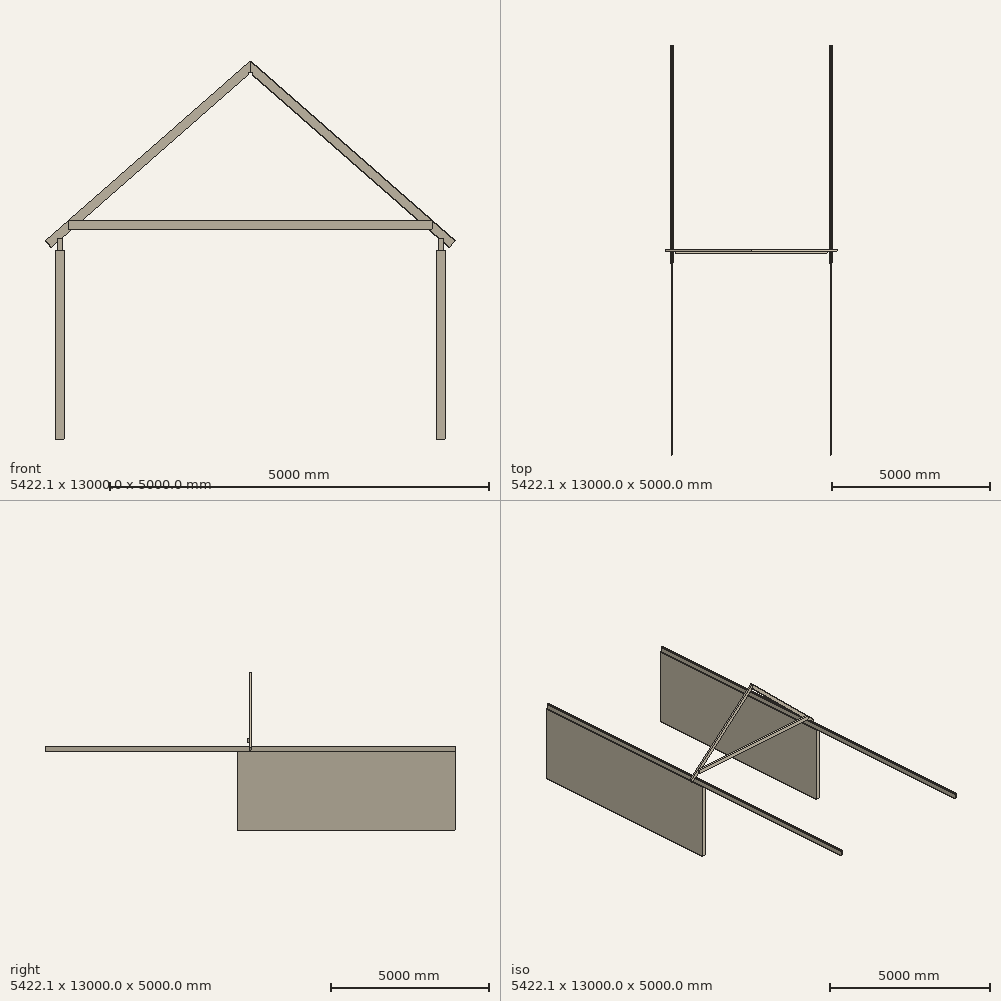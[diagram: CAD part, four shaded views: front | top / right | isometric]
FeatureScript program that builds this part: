
annotation { "Feature Type Name" : "Feature", "Feature Type Description" : "" }
export const myFeature = defineFeature(function(context is Context, id is Id, definition is map)
    precondition{}
    {
        {
            var Q0;
            Q0=qCreatedBy(makeId("Front.planeOp"),FACE);
            var sketch = newSketch(context, id + "F0", { "sketchPlane" : qUnion([Q0])});
            skLineSegment(sketch, "E0", {"start": v(0, 0) * mm, "end": v(0, 3904.1) * mm, "construction": true});
            skLineSegment(sketch, "E1", {"start": v(-3356.12, 0) * mm, "end": v(3820.43, 0) * mm, "construction": true});
            skLineSegment(sketch, "E2.bottom", {"start": v(-2550, 160) * mm, "end": v(-2490, 160) * mm});
            skLineSegment(sketch, "E2.top", {"start": v(-2550, 0) * mm, "end": v(-2490, 0) * mm});
            skLineSegment(sketch, "E2.left", {"start": v(-2550, 160) * mm, "end": v(-2550, 0) * mm});
            skLineSegment(sketch, "E2.right", {"start": v(-2490, 160) * mm, "end": v(-2490, 0) * mm});
            skLineSegment(sketch, "E3.bottom", {"start": v(2490, 160) * mm, "end": v(2550, 160) * mm});
            skLineSegment(sketch, "E3.top", {"start": v(2490, 0) * mm, "end": v(2550, 0) * mm});
            skLineSegment(sketch, "E3.left", {"start": v(2490, 160) * mm, "end": v(2490, 0) * mm});
            skLineSegment(sketch, "E3.right", {"start": v(2550, 160) * mm, "end": v(2550, 0) * mm});
            skLineSegment(sketch, "E4", {"start": v(-735.63, 2500) * mm, "end": v(730.19, 2500) * mm, "construction": true});
            skSolve(sketch);
        }
        {
            var Q0;
            Q0 = qSketchRegion(id + "F0", true);
            extrude(context, id + "F1", {"entities" : qUnion([Q0]), "endBound" : BoundingType.SYMMETRIC, "depth" : 13000 * mm, "offsetDistance" : 25 * mm});
        }
        {
            var Q0;
            Q0=makeQuery(id+"F1.opExtrude","CAP_FACE",FACE,{"disambiguationData":[OSD([sQuery(id+"F0.wireOp",EDGE,"E3.bottom"),sQuery(id+"F0.wireOp",EDGE,"E3.top"),sQuery(id+"F0.wireOp",EDGE,"E3.left"),sQuery(id+"F0.wireOp",EDGE,"E3.right")])],"isStart":true});
            var sketch = newSketch(context, id + "F2", { "sketchPlane" : qUnion([Q0])});
            skLineSegment(sketch, "E5.bottom", {"start": v(-2580, 0) * mm, "end": v(-2460, 0) * mm});
            skLineSegment(sketch, "E5.top", {"start": v(-2580, -2500) * mm, "end": v(-2460, -2500) * mm});
            skLineSegment(sketch, "E5.left", {"start": v(-2580, 0) * mm, "end": v(-2580, -2500) * mm});
            skLineSegment(sketch, "E5.right", {"start": v(-2460, 0) * mm, "end": v(-2460, -2500) * mm});
            skLineSegment(sketch, "E6.bottom", {"start": v(2460, 0) * mm, "end": v(2580, 0) * mm});
            skLineSegment(sketch, "E6.top", {"start": v(2460, -2500) * mm, "end": v(2580, -2500) * mm});
            skLineSegment(sketch, "E6.left", {"start": v(2460, 0) * mm, "end": v(2460, -2500) * mm});
            skLineSegment(sketch, "E6.right", {"start": v(2580, 0) * mm, "end": v(2580, -2500) * mm});
            skLineSegment(sketch, "E7", {"start": v(-2724.2, 0) * mm, "end": v(2884.68, 0) * mm, "construction": true});
            skPoint(sketch, "E7.startSnap0", {"position": v(-2520, 0) * mm});
            skSolve(sketch);
        }
        {
            var Q0;
            Q0 = qSketchRegion(id + "F2", true);
            extrude(context, id + "F3", {"entities" : qUnion([Q0]), "oppositeDirection" : true, "depth" : 6900 * mm, "offsetDistance" : 25 * mm});
        }
        {
            var Q0;
            Q0=qCreatedBy(makeId("Front.planeOp"),FACE);
            var sketch = newSketch(context, id + "F4", { "sketchPlane" : qUnion([Q0])});
            skLineSegment(sketch, "E8", {"start": v(-5, 2500) * mm, "end": v(-2711.05, 125.7) * mm});
            skLineSegment(sketch, "E9", {"start": v(-2711.05, 125.7) * mm, "end": v(-2631.9, 35.5) * mm});
            skLineSegment(sketch, "E10.bottom", {"start": v(-30, 2358.42) * mm, "end": v(30, 2358.42) * mm, "construction": true});
            skLineSegment(sketch, "E10.top", {"start": v(-30, 2198.42) * mm, "end": v(30, 2198.42) * mm, "construction": true});
            skLineSegment(sketch, "E10.left", {"start": v(-30, 2358.42) * mm, "end": v(-30, 2198.42) * mm, "construction": true});
            skLineSegment(sketch, "E10.right", {"start": v(30, 2358.42) * mm, "end": v(30, 2198.42) * mm, "construction": true});
            skLineSegment(sketch, "E11", {"start": v(-5, 2500) * mm, "end": v(-5, 2358.42) * mm});
            skLineSegment(sketch, "E12", {"start": v(-5, 2358.42) * mm, "end": v(-30, 2358.42) * mm});
            skLineSegment(sketch, "E13", {"start": v(-30, 2358.42) * mm, "end": v(-30, 2318.42) * mm});
            skLineSegment(sketch, "E14", {"start": v(-2550, 160) * mm, "end": v(-2550, 107.36) * mm});
            skLineSegment(sketch, "E15.trimOffspring", {"start": v(-2490, 160) * mm, "end": v(-30, 2318.42) * mm});
            skLineSegment(sketch, "E16", {"start": v(-2550, 160) * mm, "end": v(-2490, 160) * mm});
            skLineSegment(sketch, "E17", {"start": v(-2550, 107.36) * mm, "end": v(-2631.9, 35.5) * mm});
            skLineSegment(sketch, "E18.MirrorCS", {"start": v(2711.05, 125.7) * mm, "end": v(2631.9, 35.5) * mm});
            skLineSegment(sketch, "E19.MirrorCS", {"start": v(5, 2500) * mm, "end": v(2711.05, 125.7) * mm});
            skLineSegment(sketch, "E20.MirrorCS", {"start": v(2550, 107.36) * mm, "end": v(2631.9, 35.5) * mm});
            skLineSegment(sketch, "E21.MirrorCS", {"start": v(2550, 160) * mm, "end": v(2550, 107.36) * mm});
            skLineSegment(sketch, "E22.MirrorCS", {"start": v(2550, 160) * mm, "end": v(2490, 160) * mm});
            skLineSegment(sketch, "E23.MirrorCS", {"start": v(2490, 160) * mm, "end": v(30, 2318.42) * mm});
            skLineSegment(sketch, "E24.MirrorCS", {"start": v(5, 2500) * mm, "end": v(5, 2358.42) * mm});
            skLineSegment(sketch, "E25.MirrorCS", {"start": v(30, 2358.42) * mm, "end": v(-30, 2358.42) * mm, "construction": true});
            skLineSegment(sketch, "E26.MirrorCS", {"start": v(30, 2358.42) * mm, "end": v(30, 2318.42) * mm});
            skLineSegment(sketch, "E27.MirrorCS", {"start": v(5, 2358.42) * mm, "end": v(30, 2358.42) * mm});
            skSolve(sketch);
        }
        {
            var Q0;
            Q0 = qSketchRegion(id + "F4", true);
            extrude(context, id + "F5", {"entities" : qUnion([Q0]), "endBound" : BoundingType.SYMMETRIC, "depth" : 60 * mm, "offsetDistance" : 25 * mm});
        }
        {
            var Q0;
            Q0=makeQuery(id+"F5.opExtrude","CAP_FACE",FACE,{"disambiguationData":[OSD([sQuery(id+"F4.wireOp",EDGE,"E8"),sQuery(id+"F4.wireOp",EDGE,"E9"),sQuery(id+"F4.wireOp",EDGE,"E11"),sQuery(id+"F4.wireOp",EDGE,"E12"),sQuery(id+"F4.wireOp",EDGE,"E13"),sQuery(id+"F4.wireOp",EDGE,"E14"),sQuery(id+"F4.wireOp",EDGE,"E15.trimOffspring"),sQuery(id+"F4.wireOp",EDGE,"E16"),sQuery(id+"F4.wireOp",EDGE,"E17")])],"isStart":false});
            var sketch = newSketch(context, id + "F6", { "sketchPlane" : qUnion([Q0])});
            skLineSegment(sketch, "E28.bottom", {"start": v(-2400, 398.6) * mm, "end": v(2400, 398.6) * mm});
            skLineSegment(sketch, "E28.top", {"start": v(-2400, 278.6) * mm, "end": v(2400, 278.6) * mm});
            skLineSegment(sketch, "E28.left", {"start": v(-2400, 398.6) * mm, "end": v(-2400, 278.6) * mm});
            skLineSegment(sketch, "E28.right", {"start": v(2400, 398.6) * mm, "end": v(2400, 278.6) * mm});
            skPoint(sketch, "E29", {"position": v(0, 398.6) * mm});
            skSolve(sketch);
        }
        {
            var Q0;
            Q0 = qSketchRegion(id + "F6", true);
            extrude(context, id + "F7", {"entities" : qUnion([Q0]), "depth" : 60 * mm, "offsetDistance" : 25 * mm});
        }
    });
